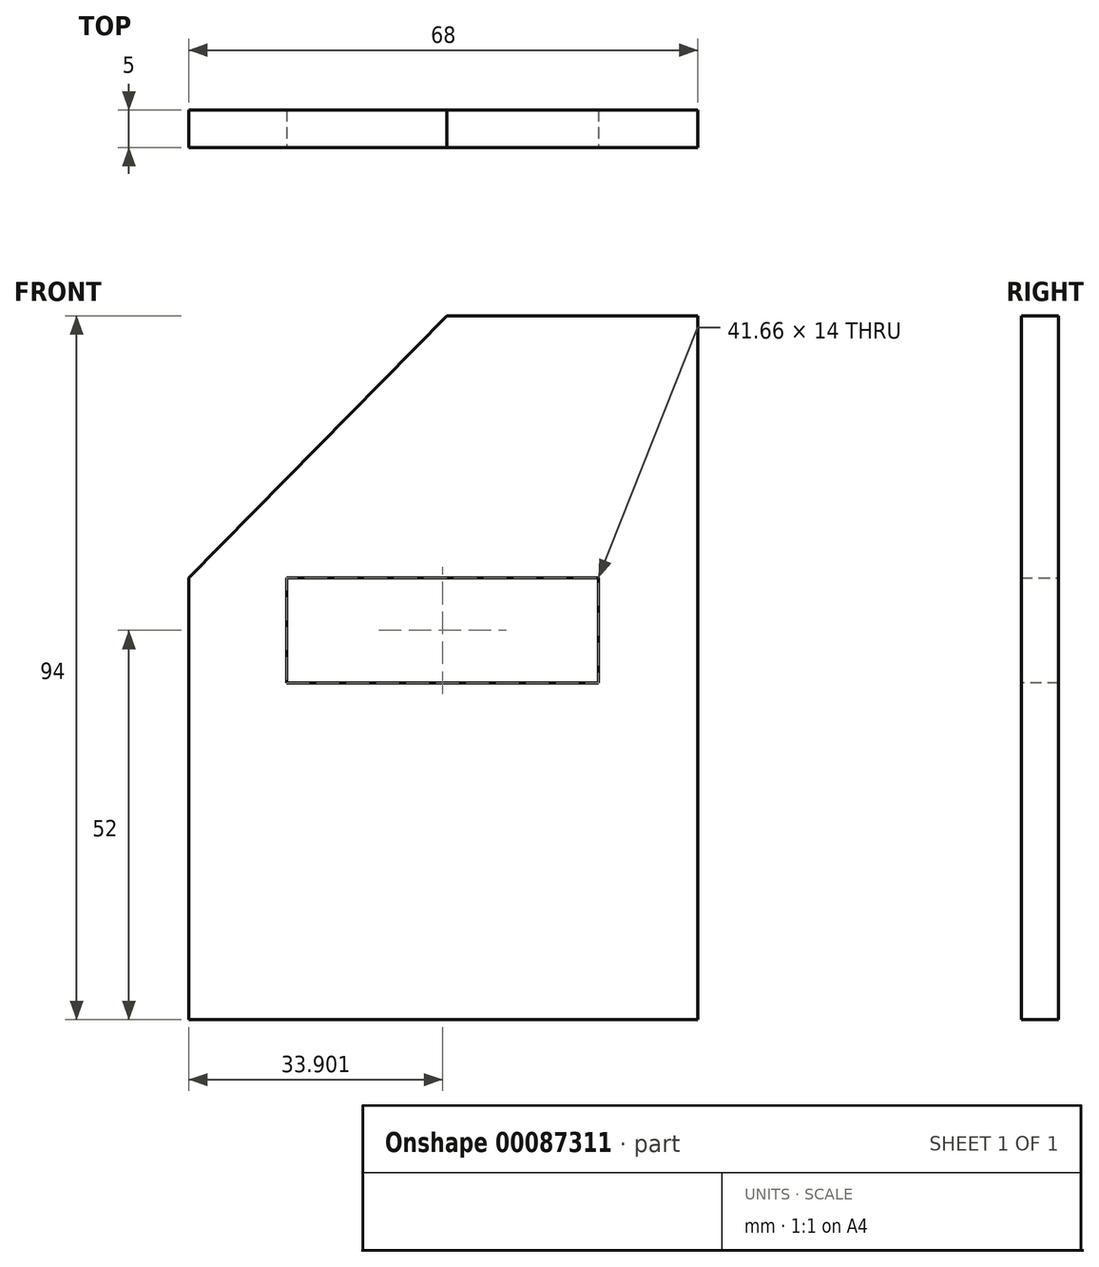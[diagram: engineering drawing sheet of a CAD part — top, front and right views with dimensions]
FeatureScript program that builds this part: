
annotation { "Feature Type Name" : "Feature", "Feature Type Description" : "" }
export const myFeature = defineFeature(function(context is Context, id is Id, definition is map)
    precondition{}
    {
        {
            var Q0;
            Q0=qCreatedBy(makeId("Front.planeOp"),FACE);
            var sketch = newSketch(context, id + "F0", { "sketchPlane" : qUnion([Q0])});
            skLineSegment(sketch, "E0", {"start": v(-34.5, -59) * mm, "end": v(33.5, -59) * mm});
            skLineSegment(sketch, "E1", {"start": v(-34.5, 0) * mm, "end": v(-34.5, -59) * mm});
            skLineSegment(sketch, "E2", {"start": v(33.5, 35) * mm, "end": v(33.5, -59) * mm});
            skLineSegment(sketch, "E3", {"start": v(33.5, 35) * mm, "end": v(0, 35) * mm});
            skLineSegment(sketch, "E4", {"start": v(0, 35) * mm, "end": v(-34.5, 0) * mm});
            skSolve(sketch);
        }
        {
            var Q0;
            Q0 = qSketchRegion(id + "F0", true);
            extrude(context, id + "F1", {"entities" : qUnion([Q0]), "endBound" : BoundingType.SYMMETRIC, "depth" : 5 * mm});
        }
        {
            var Q0;
            Q0=makeQuery(id+"F1.opExtrude","CAP_FACE",FACE,{"disambiguationData":[OSD([sQuery(id+"F0.wireOp",EDGE,"E0"),sQuery(id+"F0.wireOp",EDGE,"E1"),sQuery(id+"F0.wireOp",EDGE,"E2"),sQuery(id+"F0.wireOp",EDGE,"E3"),sQuery(id+"F0.wireOp",EDGE,"E4")])],"isStart":false});
            var sketch = newSketch(context, id + "F2", { "sketchPlane" : qUnion([Q0])});
            skLineSegment(sketch, "E5.bottom", {"start": v(-21.43, 0) * mm, "end": v(20.23, 0) * mm});
            skLineSegment(sketch, "E5.top", {"start": v(-21.43, -14) * mm, "end": v(20.23, -14) * mm});
            skLineSegment(sketch, "E5.left", {"start": v(-21.43, 0) * mm, "end": v(-21.43, -14) * mm});
            skLineSegment(sketch, "E5.right", {"start": v(20.23, 0) * mm, "end": v(20.23, -14) * mm});
            skSolve(sketch);
        }
        {
            var Q0;
            Q0 = qSketchRegion(id + "F2", true);
            extrude(context, id + "F3", {"entities" : qUnion([Q0]), "operationType" : NewBodyOperationType.REMOVE, "oppositeDirection" : true, "depth" : 25 * mm});
        }
    });
